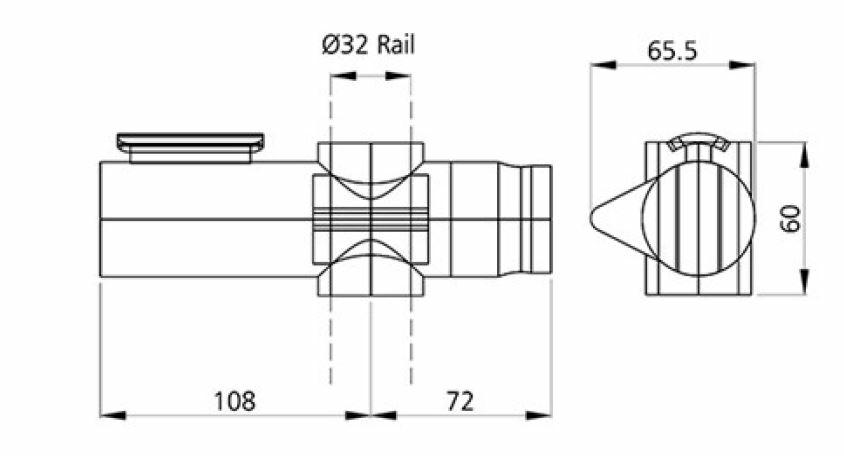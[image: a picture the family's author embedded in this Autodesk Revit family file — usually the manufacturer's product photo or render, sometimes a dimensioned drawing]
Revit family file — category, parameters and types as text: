
# Revit family: RBA4801-721
name_source: partatom
category: Plumbing Fixtures
units: mm (PartAtom-declared; Revit-internal decimal feet)

## family parameters
Always vertical = Yes
Cut with Voids When Loaded = No
Part Type = Normal
Room Calculation Point = No
Round Connector Dimension = Use Diameter
Shared = Yes
Work Plane-Based = No

## types (1)
- RBA4801-721
    CW Connection = Yes
    Default Elevation = 0 mm  [stored 0 ft]
    Description = Modular Shower T-Rail Kit, Satin
    Distance Away from Toilet (default) = 1090 mm  [stored 3.57612 ft]
    Distance Away from Wall (default) = 100 mm  [stored 0.328084 ft]
    HW Connection = Yes
    Manufacturer = RBA Group
    Materials and Finishes = Stainless Steel Satin Finish
    Model = RBA4801-721
    OFFSET = 1000 mm  [stored 3.28084 ft]
    URL = www.rba.com.au
    Vent Connection = Yes
    Waste Connection = Yes

note: [stored X ft] marks values corroborated as IEEE doubles in the binary element streams (Revit-internal decimal feet)

## geometry (parser evidence)
native form markers: Blend x4, Sweep x13
no freeform markers — native parametric forms only
